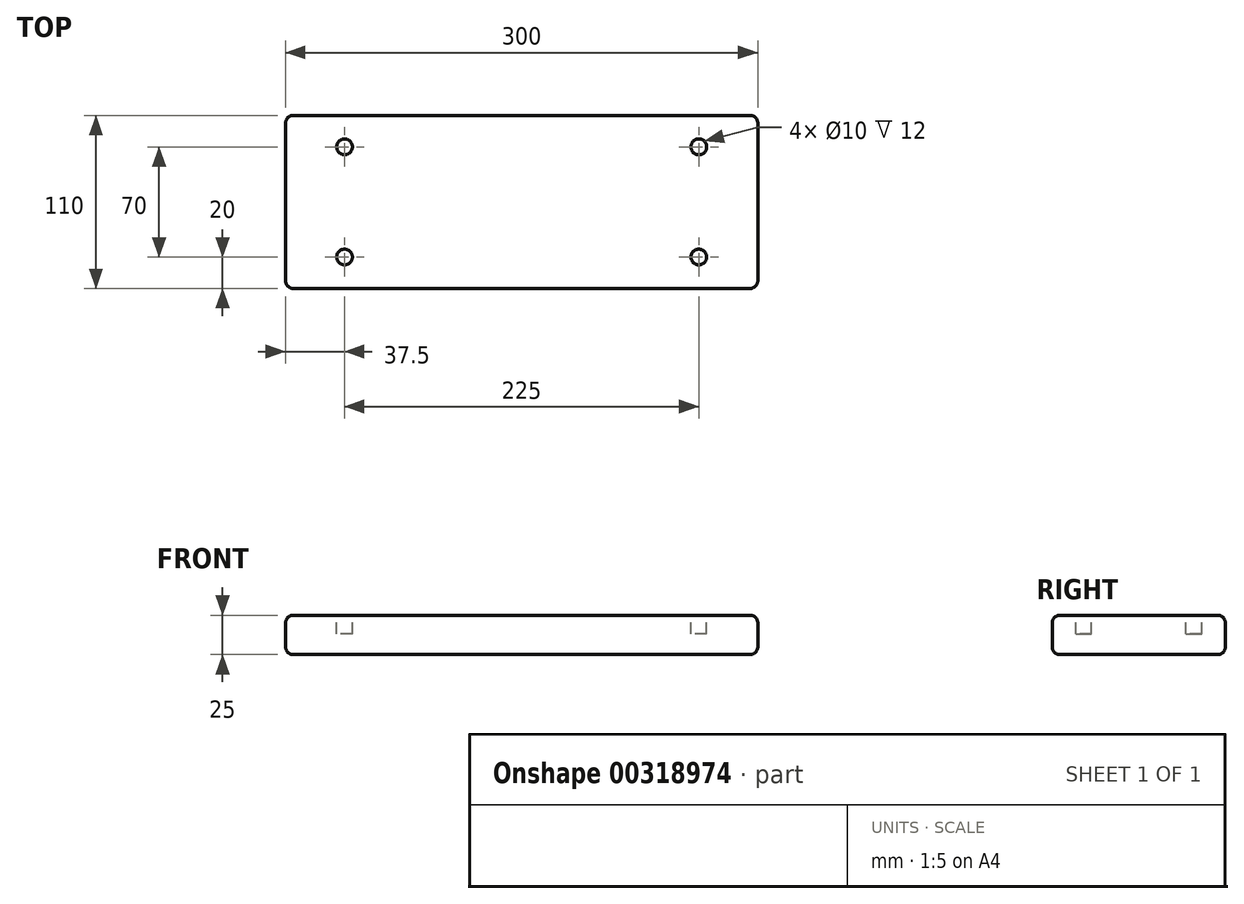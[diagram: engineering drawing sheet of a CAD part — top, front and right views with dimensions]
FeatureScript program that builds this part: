
annotation { "Feature Type Name" : "Feature", "Feature Type Description" : "" }
export const myFeature = defineFeature(function(context is Context, id is Id, definition is map)
    precondition{}
    {
        {
            var Q0;
            Q0=qCreatedBy(makeId("Top.planeOp"),FACE);
            var sketch = newSketch(context, id + "F0", { "sketchPlane" : qUnion([Q0])});
            skLineSegment(sketch, "E0.bottom", {"start": v(0, 0) * mm, "end": v(-300, 0) * mm});
            skLineSegment(sketch, "E0.top", {"start": v(0, 110) * mm, "end": v(-300, 110) * mm});
            skLineSegment(sketch, "E0.left", {"start": v(0, 0) * mm, "end": v(0, 110) * mm});
            skLineSegment(sketch, "E0.right", {"start": v(-300, 0) * mm, "end": v(-300, 110) * mm});
            skSolve(sketch);
        }
        {
            var Q0;
            Q0 = qSketchRegion(id + "F0", true);
            extrude(context, id + "F1", {"entities" : qUnion([Q0]), "depth" : 25 * mm});
        }
        {
            var Q0;
            Q0=makeQuery(id+"F1.opExtrude","CAP_FACE",FACE,{"disambiguationData":[OSD([sQuery(id+"F0.wireOp",EDGE,"E0.bottom"),sQuery(id+"F0.wireOp",EDGE,"E0.top"),sQuery(id+"F0.wireOp",EDGE,"E0.left"),sQuery(id+"F0.wireOp",EDGE,"E0.right")])],"isStart":false});
            var sketch = newSketch(context, id + "F2", { "sketchPlane" : qUnion([Q0])});
            skLineSegment(sketch, "E1", {"start": v(-300, 90) * mm, "end": v(-262.5, 90) * mm, "construction": true});
            skLineSegment(sketch, "E2", {"start": v(-262.5, 90) * mm, "end": v(-262.5, 110) * mm, "construction": true});
            skPoint(sketch, "E3.startSnap0", {"position": v(-150, 110) * mm});
            skPoint(sketch, "E3.endSnap0", {"position": v(-150, 0) * mm});
            skLineSegment(sketch, "E4", {"start": v(0, 55) * mm, "end": v(-339.05, 55) * mm, "construction": true});
            skPoint(sketch, "E4.endSnap0", {"position": v(0, 55) * mm});
            skCircle(sketch, "E5", {"center": v(-262.5, 90) * mm, "radius": 5 * mm});
            skCircle(sketch, "E6.MirrorC", {"center": v(-262.5, 20) * mm, "radius": 5 * mm});
            skLineSegment(sketch, "E7.MirrorCS", {"start": v(-150, -43.45) * mm, "end": v(-150, 152.33) * mm, "construction": true});
            skCircle(sketch, "E8.MirrorC", {"center": v(-37.5, 90) * mm, "radius": 5 * mm});
            skCircle(sketch, "E9.MirrorC", {"center": v(-37.5, 20) * mm, "radius": 5 * mm});
            skSolve(sketch);
        }
        {
            var Q0;
            Q0 = qSketchRegion(id + "F2", true);
            extrude(context, id + "F3", {"entities" : qUnion([Q0]), "operationType" : NewBodyOperationType.REMOVE, "oppositeDirection" : true, "depth" : 12 * mm});
        }
        {
            var Q0;
            Q0=makeQuery(id+"F1.opExtrude","SWEPT_FACE",FACE,{"disambiguationData":[OSD([sQuery(id+"F0.wireOp",EDGE,"E0.top")])]});
            var Q1;
            Q1=makeQuery(id+"F1.opExtrude","SWEPT_FACE",FACE,{"disambiguationData":[OSD([sQuery(id+"F0.wireOp",EDGE,"E0.right")])]});
            var Q2;
            Q2=makeQuery(id+"F1.opExtrude","SWEPT_FACE",FACE,{"disambiguationData":[OSD([sQuery(id+"F0.wireOp",EDGE,"E0.bottom")])]});
            var Q3;
            Q3=makeQuery(id+"F1.opExtrude","SWEPT_FACE",FACE,{"disambiguationData":[OSD([sQuery(id+"F0.wireOp",EDGE,"E0.left")])]});
            fillet(context, id + "F4", {"entities" : qUnion([Q0, Q1, Q2, Q3]), "radius" : 5 * mm, "tangentPropagation" : true, "allowEdgeOverflow" : false});
        }
    });
